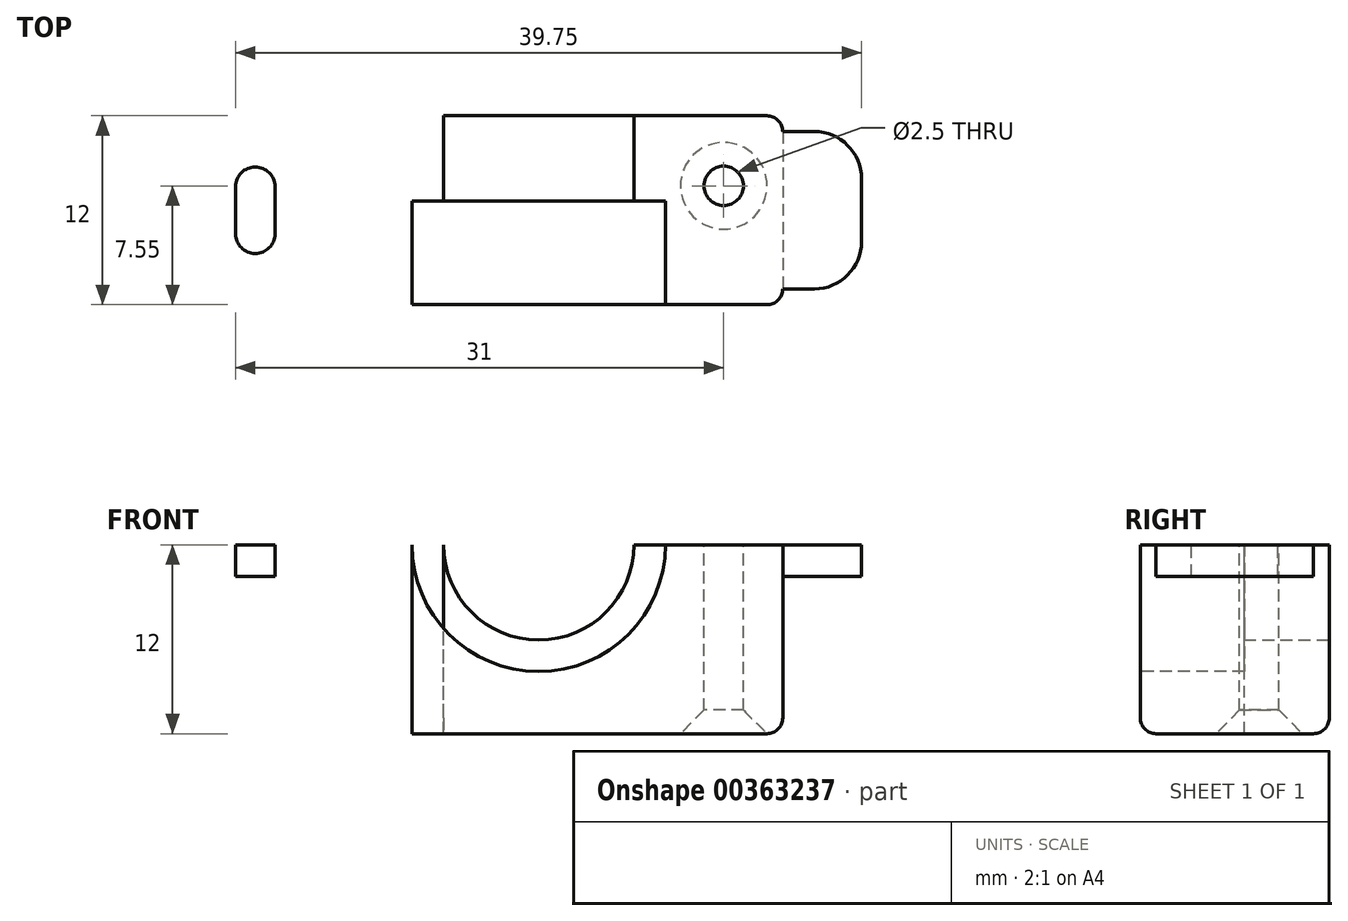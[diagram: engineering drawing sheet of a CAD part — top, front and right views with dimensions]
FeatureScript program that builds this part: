
annotation { "Feature Type Name" : "Feature", "Feature Type Description" : "" }
export const myFeature = defineFeature(function(context is Context, id is Id, definition is map)
    precondition{}
    {
        {
            var Q0;
            Q0=qCreatedBy(makeId("Top.planeOp"),FACE);
            var sketch = newSketch(context, id + "F0", { "sketchPlane" : qUnion([Q0])});
            skLineSegment(sketch, "E0.bottom", {"start": v(0, 0) * mm, "end": v(25, 0) * mm});
            skLineSegment(sketch, "E0.top", {"start": v(0, 12) * mm, "end": v(25, 12) * mm});
            skLineSegment(sketch, "E0.left", {"start": v(0, 0) * mm, "end": v(0, 12) * mm});
            skLineSegment(sketch, "E0.right", {"start": v(25, 0) * mm, "end": v(25, 12) * mm});
            skSolve(sketch);
        }
        {
            var Q0;
            Q0=qSketchRegion(id+"F0",true);
            extrude(context, id + "F1", {"entities" : qUnion([Q0]), "depth" : 12 * mm});
        }
        {
            var Q0;
            Q0=makeQuery(id+"F1.opExtrude","SWEPT_FACE",FACE,{"disambiguationData":[OSD([sQuery(id+"F0.wireOp",EDGE,"E0.bottom")])]});
            var sketch = newSketch(context, id + "F2", { "sketchPlane" : qUnion([Q0])});
            skCircle(sketch, "E1", {"center": v(12.5, 12) * mm, "radius": 8.05 * mm});
            skSolve(sketch);
        }
        {
            var Q0;
            Q0=qSketchRegion(id+"F2",true);
            extrude(context, id + "F3", {"entities" : qUnion([Q0]), "operationType" : NewBodyOperationType.REMOVE, "oppositeDirection" : true, "depth" : 6.6 * mm});
        }
        {
            var Q0;
            Q0=makeQuery(id+"F1.opExtrude","SWEPT_FACE",FACE,{"disambiguationData":[OSD([sQuery(id+"F0.wireOp",EDGE,"E0.top")])]});
            var sketch = newSketch(context, id + "F4", { "sketchPlane" : qUnion([Q0])});
            skCircle(sketch, "E2", {"center": v(-12.5, 12) * mm, "radius": 6.05 * mm});
            skSolve(sketch);
        }
        {
            var Q0;
            Q0=qSketchRegion(id+"F4",true);
            extrude(context, id + "F5", {"entities" : qUnion([Q0]), "operationType" : NewBodyOperationType.REMOVE, "oppositeDirection" : true, "depth" : 5.4 * mm});
        }
        {
            var Q0;
            Q0=makeQuery(id+"F1.opExtrude","SWEPT_FACE",FACE,{"disambiguationData":[OSD([sQuery(id+"F0.wireOp",EDGE,"E0.left")])]});
            var sketch = newSketch(context, id + "F6", { "sketchPlane" : qUnion([Q0])});
            skLineSegment(sketch, "E3.bottom", {"start": v(-12, 0) * mm, "end": v(0, 0) * mm});
            skLineSegment(sketch, "E3.top", {"start": v(-12, 12) * mm, "end": v(0, 12) * mm});
            skLineSegment(sketch, "E3.left", {"start": v(-12, 0) * mm, "end": v(-12, 12) * mm});
            skLineSegment(sketch, "E3.right", {"start": v(0, 0) * mm, "end": v(0, 12) * mm});
            skSolve(sketch);
        }
        {
            var Q0;
            Q0=qSketchRegion(id+"F6",true);
            extrude(context, id + "F7", {"entities" : qUnion([Q0]), "operationType" : NewBodyOperationType.ADD, "depth" : 3 * mm});
        }
        {
            var Q0;
            Q0=makeQuery(id+"F1.opExtrude","SWEPT_FACE",FACE,{"disambiguationData":[OSD([sQuery(id+"F0.wireOp",EDGE,"E0.right")])]});
            var sketch = newSketch(context, id + "F8", { "sketchPlane" : qUnion([Q0])});
            skLineSegment(sketch, "E4.bottom", {"start": v(12, 12) * mm, "end": v(0, 12) * mm});
            skLineSegment(sketch, "E4.top", {"start": v(12, 0) * mm, "end": v(0, 0) * mm});
            skLineSegment(sketch, "E4.left", {"start": v(12, 12) * mm, "end": v(12, 0) * mm});
            skLineSegment(sketch, "E4.right", {"start": v(0, 12) * mm, "end": v(0, 0) * mm});
            skSolve(sketch);
        }
        {
            var Q0;
            Q0=qSketchRegion(id+"F8",true);
            extrude(context, id + "F9", {"entities" : qUnion([Q0]), "operationType" : NewBodyOperationType.ADD, "depth" : 3 * mm});
        }
        {
            var Q0;
            {var subQ0=sQuery(id+"F0.wireOp",EDGE,"E0.bottom");var subQ1=sQuery(id+"F0.wireOp",EDGE,"E0.top");var subQ2=sQuery(id+"F0.wireOp",EDGE,"E0.left");Q0=makeQuery(id+"F5.boolean.opBoolean","SPLIT",FACE,{"disambiguationData":[TD([makeQuery(id+"F1.opExtrude","SWEPT_FACE",FACE,{"disambiguationData":[OSD([subQ2])]})])],"derivedFrom":makeQuery(id+"F1.opExtrude","CAP_FACE",FACE,{"disambiguationData":[OSD([subQ0,subQ1,subQ2,sQuery(id+"F0.wireOp",EDGE,"E0.right")])],"isStart":false})});}
            var sketch = newSketch(context, id + "F10", { "sketchPlane" : qUnion([Q0])});
            skCircle(sketch, "E5", {"center": v(0.75, 7.55) * mm, "radius": 1.25 * mm});
            skCircle(sketch, "E6", {"center": v(24.25, 7.55) * mm, "radius": 1.25 * mm});
            skSolve(sketch);
        }
        {
            var Q0;
            Q0=qSketchRegion(id+"F10",true);
            extrude(context, id + "F11", {"entities" : qUnion([Q0]), "operationType" : NewBodyOperationType.REMOVE, "oppositeDirection" : true, "depth" : 25 * mm});
        }
        {
            var Q0;
            Q0=makeQuery(id+"F11.boolean.opBoolean","INTERSECT",EDGE,{"derivedFrom":[makeQuery(id+"F9.boolean.opBoolean","MERGE",FACE,{"derivedFrom":[makeQuery(id+"F7.boolean.opBoolean","MERGE",FACE,{"derivedFrom":[makeQuery(id+"F1.opExtrude","CAP_FACE",FACE,{"disambiguationData":[OSD([sQuery(id+"F0.wireOp",EDGE,"E0.bottom"),sQuery(id+"F0.wireOp",EDGE,"E0.top"),sQuery(id+"F0.wireOp",EDGE,"E0.left"),sQuery(id+"F0.wireOp",EDGE,"E0.right")])],"isStart":true}),makeQuery(id+"F7.opExtrude","SWEPT_FACE",FACE,{"disambiguationData":[OSD([sQuery(id+"F6.wireOp",EDGE,"E3.bottom")])]})]}),makeQuery(id+"F9.opExtrude","SWEPT_FACE",FACE,{"disambiguationData":[OSD([sQuery(id+"F8.wireOp",EDGE,"E4.top")])]})]}),makeQuery(id+"F11.opExtrude","SWEPT_FACE",FACE,{"disambiguationData":[OSD([sQuery(id+"F10.wireOp",EDGE,"E6")])]})]});
            var Q1;
            Q1=makeQuery(id+"F11.boolean.opBoolean","INTERSECT",EDGE,{"derivedFrom":[makeQuery(id+"F9.boolean.opBoolean","MERGE",FACE,{"derivedFrom":[makeQuery(id+"F7.boolean.opBoolean","MERGE",FACE,{"derivedFrom":[makeQuery(id+"F1.opExtrude","CAP_FACE",FACE,{"disambiguationData":[OSD([sQuery(id+"F0.wireOp",EDGE,"E0.bottom"),sQuery(id+"F0.wireOp",EDGE,"E0.top"),sQuery(id+"F0.wireOp",EDGE,"E0.left"),sQuery(id+"F0.wireOp",EDGE,"E0.right")])],"isStart":true}),makeQuery(id+"F7.opExtrude","SWEPT_FACE",FACE,{"disambiguationData":[OSD([sQuery(id+"F6.wireOp",EDGE,"E3.bottom")])]})]}),makeQuery(id+"F9.opExtrude","SWEPT_FACE",FACE,{"disambiguationData":[OSD([sQuery(id+"F8.wireOp",EDGE,"E4.top")])]})]}),makeQuery(id+"F11.opExtrude","SWEPT_FACE",FACE,{"disambiguationData":[OSD([sQuery(id+"F10.wireOp",EDGE,"E5")])]})]});
            chamfer(context, id + "F12", {"entities" : qUnion([Q0, Q1]), "width" : 1.5 * mm, "tangentPropagation" : true});
        }
        {
            var Q0;
            Q0=makeQuery(id+"F9.opExtrude","CAP_EDGE",EDGE,{"disambiguationData":[OSD([sQuery(id+"F8.wireOp",EDGE,"E4.top")])],"isStart":false});
            var Q1;
            Q1=makeQuery(id+"F7.opExtrude","CAP_EDGE",EDGE,{"disambiguationData":[OSD([sQuery(id+"F6.wireOp",EDGE,"E3.bottom")])],"isStart":false});
            var Q2;
            Q2=makeQuery(id+"F9.opExtrude","CAP_EDGE",EDGE,{"disambiguationData":[OSD([sQuery(id+"F8.wireOp",EDGE,"E4.left")])],"isStart":false});
            var Q3;
            Q3=makeQuery(id+"F9.boolean.opBoolean","MERGE",EDGE,{"derivedFrom":[makeQuery(id+"F7.boolean.opBoolean","MERGE",EDGE,{"derivedFrom":[makeQuery(id+"F1.opExtrude","CAP_EDGE",EDGE,{"disambiguationData":[OSD([sQuery(id+"F0.wireOp",EDGE,"E0.top")])],"isStart":true}),makeQuery(id+"F7.opExtrude","SWEPT_EDGE",EDGE,{"disambiguationData":[OSD([sQuery(id+"F6.wireOp",EDGE,"E3.bottom"),sQuery(id+"F6.wireOp",EDGE,"E3.left")])]})]}),makeQuery(id+"F9.opExtrude","SWEPT_EDGE",EDGE,{"disambiguationData":[OSD([sQuery(id+"F8.wireOp",EDGE,"E4.top"),sQuery(id+"F8.wireOp",EDGE,"E4.left")])]})]});
            var Q4;
            Q4=makeQuery(id+"F7.opExtrude","CAP_EDGE",EDGE,{"disambiguationData":[OSD([sQuery(id+"F6.wireOp",EDGE,"E3.left")])],"isStart":false});
            var Q5;
            Q5=makeQuery(id+"F7.opExtrude","CAP_EDGE",EDGE,{"disambiguationData":[OSD([sQuery(id+"F6.wireOp",EDGE,"E3.right")])],"isStart":false});
            var Q6;
            Q6=makeQuery(id+"F9.boolean.opBoolean","MERGE",EDGE,{"derivedFrom":[makeQuery(id+"F7.boolean.opBoolean","MERGE",EDGE,{"derivedFrom":[makeQuery(id+"F1.opExtrude","CAP_EDGE",EDGE,{"disambiguationData":[OSD([sQuery(id+"F0.wireOp",EDGE,"E0.bottom")])],"isStart":true}),makeQuery(id+"F7.opExtrude","SWEPT_EDGE",EDGE,{"disambiguationData":[OSD([sQuery(id+"F6.wireOp",EDGE,"E3.bottom"),sQuery(id+"F6.wireOp",EDGE,"E3.right")])]})]}),makeQuery(id+"F9.opExtrude","SWEPT_EDGE",EDGE,{"disambiguationData":[OSD([sQuery(id+"F8.wireOp",EDGE,"E4.top"),sQuery(id+"F8.wireOp",EDGE,"E4.right")])]})]});
            var Q7;
            Q7=makeQuery(id+"F9.opExtrude","CAP_EDGE",EDGE,{"disambiguationData":[OSD([sQuery(id+"F8.wireOp",EDGE,"E4.right")])],"isStart":false});
            fillet(context, id + "F13", {"entities" : qUnion([Q0, Q1, Q2, Q3, Q4, Q5, Q6, Q7]), "radius" : 1 * mm, "tangentPropagation" : true, "allowEdgeOverflow" : false});
        }
        {
            var Q0;
            Q0=makeQuery(id+"F9.opExtrude","CAP_FACE",FACE,{"disambiguationData":[OSD([sQuery(id+"F8.wireOp",EDGE,"E4.bottom"),sQuery(id+"F8.wireOp",EDGE,"E4.top"),sQuery(id+"F8.wireOp",EDGE,"E4.left"),sQuery(id+"F8.wireOp",EDGE,"E4.right")])],"isStart":false});
            var sketch = newSketch(context, id + "F14", { "sketchPlane" : qUnion([Q0])});
            skLineSegment(sketch, "E7.bottom", {"start": v(11, 12) * mm, "end": v(1, 12) * mm});
            skLineSegment(sketch, "E7.top", {"start": v(11, 10) * mm, "end": v(1, 10) * mm});
            skLineSegment(sketch, "E7.left", {"start": v(11, 12) * mm, "end": v(11, 10) * mm});
            skLineSegment(sketch, "E7.right", {"start": v(1, 12) * mm, "end": v(1, 10) * mm});
            skSolve(sketch);
        }
        {
            var Q0;
            Q0=makeQuery(id+"F14.imprint","IMPRINT",FACE,{"disambiguationData":[TD([[makeQuery(id+"F14.imprint","IMPRINT",EDGE,{"derivedFrom":sQuery(id+"F14.wireOp",EDGE,"E7.bottom")}),-1.0]])]});
            extrude(context, id + "F15", {"entities" : qUnion([Q0]), "operationType" : NewBodyOperationType.ADD, "depth" : 5 * mm});
        }
        {
            var Q0;
            Q0=makeQuery(id+"F7.opExtrude","CAP_FACE",FACE,{"disambiguationData":[OSD([sQuery(id+"F6.wireOp",EDGE,"E3.bottom"),sQuery(id+"F6.wireOp",EDGE,"E3.top"),sQuery(id+"F6.wireOp",EDGE,"E3.left"),sQuery(id+"F6.wireOp",EDGE,"E3.right")])],"isStart":false});
            var sketch = newSketch(context, id + "F16", { "sketchPlane" : qUnion([Q0])});
            skLineSegment(sketch, "E8.bottom", {"start": v(-11, 12) * mm, "end": v(-1, 12) * mm});
            skLineSegment(sketch, "E8.top", {"start": v(-11, 10) * mm, "end": v(-1, 10) * mm});
            skLineSegment(sketch, "E8.left", {"start": v(-11, 12) * mm, "end": v(-11, 10) * mm});
            skLineSegment(sketch, "E8.right", {"start": v(-1, 12) * mm, "end": v(-1, 10) * mm});
            skSolve(sketch);
        }
        {
            var Q0;
            Q0=makeQuery(id+"F16.imprint","IMPRINT",FACE,{"disambiguationData":[TD([[makeQuery(id+"F16.imprint","IMPRINT",EDGE,{"derivedFrom":sQuery(id+"F16.wireOp",EDGE,"E8.bottom")}),1.0]])]});
            extrude(context, id + "F17", {"entities" : qUnion([Q0]), "operationType" : NewBodyOperationType.ADD, "depth" : 5 * mm});
        }
        {
            var Q0;
            {var subQ1=sQuery(id+"F0.wireOp",EDGE,"E0.left");var subQ2=sQuery(id+"F0.wireOp",EDGE,"E0.top");var subQ3=sQuery(id+"F0.wireOp",EDGE,"E0.bottom");Q0=makeQuery(id+"F17.boolean.opBoolean","MERGE",FACE,{"derivedFrom":[makeQuery(id+"F7.boolean.opBoolean","MERGE",FACE,{"derivedFrom":[makeQuery(id+"F5.boolean.opBoolean","SPLIT",FACE,{"disambiguationData":[TD([makeQuery(id+"F1.opExtrude","SWEPT_FACE",FACE,{"disambiguationData":[OSD([subQ1])]})])],"derivedFrom":makeQuery(id+"F1.opExtrude","CAP_FACE",FACE,{"disambiguationData":[OSD([subQ3,subQ2,subQ1,sQuery(id+"F0.wireOp",EDGE,"E0.right")])],"isStart":false})}),makeQuery(id+"F7.opExtrude","SWEPT_FACE",FACE,{"disambiguationData":[OSD([sQuery(id+"F6.wireOp",EDGE,"E3.top")])]})]}),makeQuery(id+"F17.opExtrude","SWEPT_FACE",FACE,{"disambiguationData":[OSD([sQuery(id+"F16.wireOp",EDGE,"E8.bottom")])]})]});}
            var sketch = newSketch(context, id + "F18", { "sketchPlane" : qUnion([Q0])});
            skLineSegment(sketch, "E9", {"start": v(-5.5, 7.5) * mm, "end": v(-5.5, 4.5) * mm, "construction": true});
            skLineSegment(sketch, "E10", {"start": v(30.5, 7.5) * mm, "end": v(30.5, 4.5) * mm, "construction": true});
            skArc(sketch, "E11.0.startCap", {"start": v(-6.75, 7.5) * mm, "mid": v(-5.5, 8.75) * mm, "end": v(-4.25, 7.5) * mm});
            skArc(sketch, "E11.0.endCap", {"start": v(-4.25, 4.5) * mm, "mid": v(-5.5, 3.25) * mm, "end": v(-6.75, 4.5) * mm});
            skLineSegment(sketch, "E11.0.left", {"start": v(-4.25, 7.5) * mm, "end": v(-4.25, 4.5) * mm});
            skLineSegment(sketch, "E11.0.right", {"start": v(-6.75, 7.5) * mm, "end": v(-6.75, 4.5) * mm});
            skArc(sketch, "E12.0.startCap", {"start": v(29.25, 7.5) * mm, "mid": v(30.5, 8.75) * mm, "end": v(31.75, 7.5) * mm});
            skArc(sketch, "E12.0.endCap", {"start": v(31.75, 4.5) * mm, "mid": v(30.5, 3.25) * mm, "end": v(29.25, 4.5) * mm});
            skLineSegment(sketch, "E12.0.left", {"start": v(31.75, 7.5) * mm, "end": v(31.75, 4.5) * mm});
            skLineSegment(sketch, "E12.0.right", {"start": v(29.25, 7.5) * mm, "end": v(29.25, 4.5) * mm});
            skPoint(sketch, "E13", {"position": v(-5.5, 6) * mm});
            skSolve(sketch);
        }
        {
            var Q0;
            Q0=makeQuery(id+"F18.imprint","IMPRINT",FACE,{"disambiguationData":[TD([[makeQuery(id+"F18.imprint","IMPRINT",EDGE,{"derivedFrom":sQuery(id+"F18.wireOp",EDGE,"E11.0.startCap")}),-1.0]])]});
            var Q1;
            Q1=makeQuery(id+"F18.imprint","IMPRINT",FACE,{"disambiguationData":[TD([[makeQuery(id+"F18.imprint","IMPRINT",EDGE,{"derivedFrom":sQuery(id+"F18.wireOp",EDGE,"E12.0.startCap")}),-1.0]])]});
            extrude(context, id + "F19", {"entities" : qUnion([Q0, Q1]), "operationType" : NewBodyOperationType.REMOVE, "endBound" : BoundingType.UP_TO_NEXT, "oppositeDirection" : true, "depth" : 25 * mm});
        }
        {
            var Q0;
            Q0=makeQuery(id+"F17.opExtrude","CAP_EDGE",EDGE,{"disambiguationData":[OSD([sQuery(id+"F16.wireOp",EDGE,"E8.left")])],"isStart":false});
            var Q1;
            Q1=makeQuery(id+"F17.opExtrude","CAP_EDGE",EDGE,{"disambiguationData":[OSD([sQuery(id+"F16.wireOp",EDGE,"E8.right")])],"isStart":false});
            var Q2;
            Q2=makeQuery(id+"F15.opExtrude","CAP_EDGE",EDGE,{"disambiguationData":[OSD([sQuery(id+"F14.wireOp",EDGE,"E7.left")])],"isStart":false});
            var Q3;
            Q3=makeQuery(id+"F15.opExtrude","CAP_EDGE",EDGE,{"disambiguationData":[OSD([sQuery(id+"F14.wireOp",EDGE,"E7.right")])],"isStart":false});
            fillet(context, id + "F20", {"entities" : qUnion([Q0, Q1, Q2, Q3]), "radius" : 3 * mm, "tangentPropagation" : true, "allowEdgeOverflow" : false});
        }
    });
